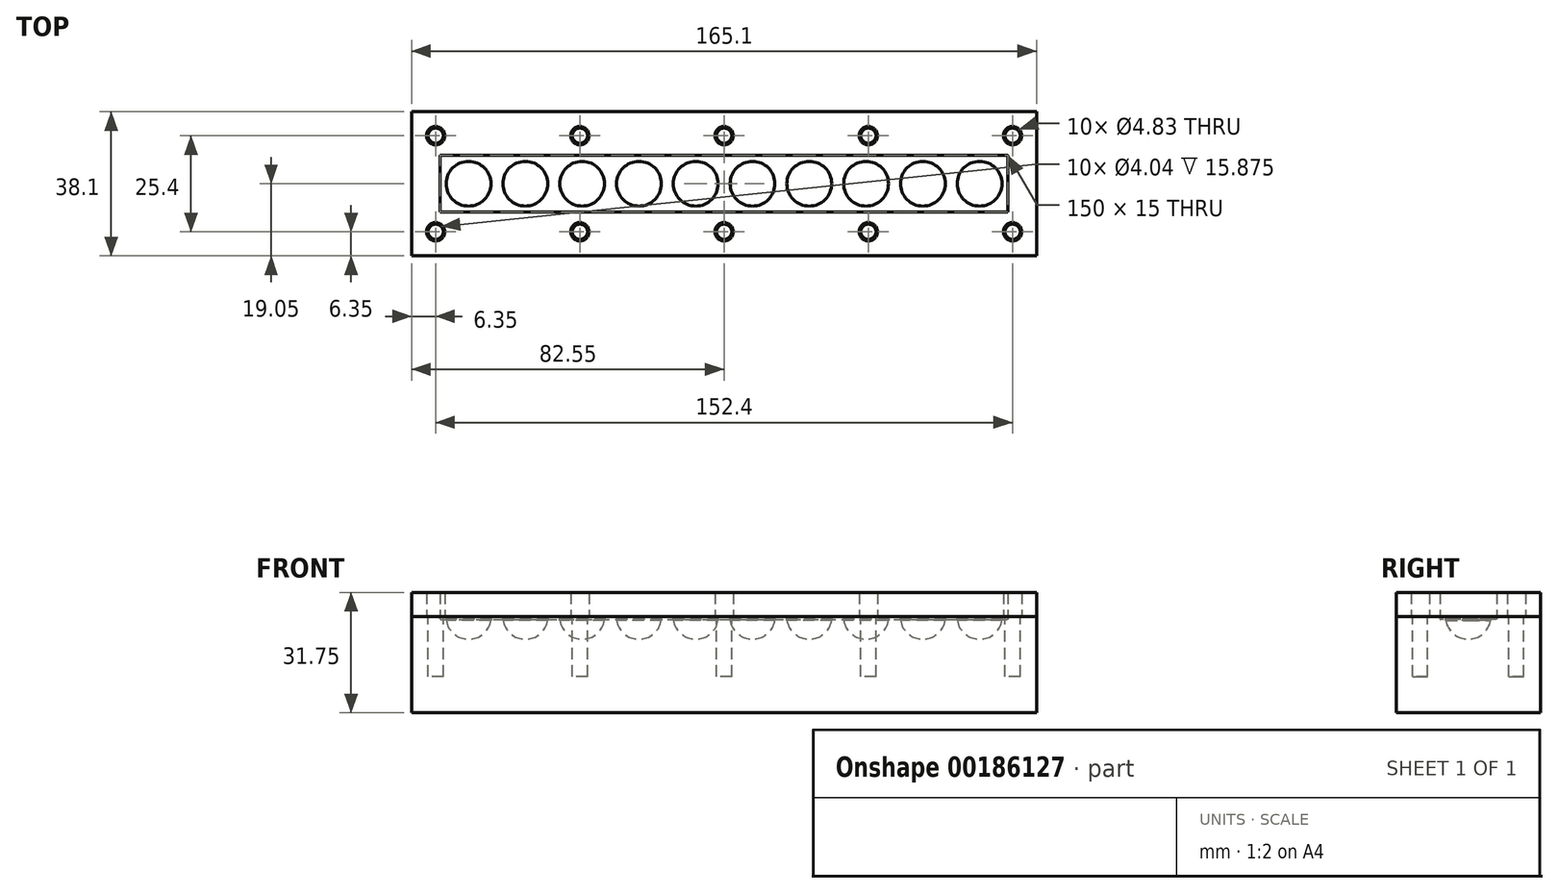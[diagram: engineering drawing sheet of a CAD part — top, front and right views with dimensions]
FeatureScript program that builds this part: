
annotation { "Feature Type Name" : "Feature", "Feature Type Description" : "" }
export const myFeature = defineFeature(function(context is Context, id is Id, definition is map)
    precondition{}
    {
        {
            var Q0;
            Q0=qCreatedBy(makeId("Top.planeOp"),FACE);
            var sketch = newSketch(context, id + "F0", { "sketchPlane" : qUnion([Q0])});
            skLineSegment(sketch, "E0.bottom", {"start": v(0, 0) * mm, "end": v(165.1, 0) * mm});
            skLineSegment(sketch, "E0.top", {"start": v(0, 38.1) * mm, "end": v(165.1, 38.1) * mm});
            skLineSegment(sketch, "E0.left", {"start": v(0, 0) * mm, "end": v(0, 38.1) * mm});
            skLineSegment(sketch, "E0.right", {"start": v(165.1, 0) * mm, "end": v(165.1, 38.1) * mm});
            skSolve(sketch);
        }
        {
            var Q0;
            Q0 = qSketchRegion(id + "F0", true);
            extrude(context, id + "F1", {"entities" : qUnion([Q0]), "depth" : 25.4 * mm});
        }
        {
            var Q0;
            Q0=makeQuery(id+"F1.opExtrude","SWEPT_FACE",FACE,{"disambiguationData":[OSD([sQuery(id+"F0.wireOp",EDGE,"E0.bottom")])]});
            var Q1;
            Q1=makeQuery(id+"F1.opExtrude","SWEPT_FACE",FACE,{"disambiguationData":[OSD([sQuery(id+"F0.wireOp",EDGE,"E0.top")])]});
            cPlane(context, id + "F2", {"entities" : qUnion([Q0, Q1]), "cplaneType" : CPlaneType.MID_PLANE, "offset" : 25.4 * mm, "width" : 152.4 * mm, "height" : 152.4 * mm});
        }
        {
            var Q0;
            Q0=qCreatedBy(id+"F2.planeOp",FACE);
            var sketch = newSketch(context, id + "F3", { "sketchPlane" : qUnion([Q0])});
            skCircle(sketch, "E1", {"center": v(15.05, 25.4) * mm, "radius": 6 * mm});
            skCircle(sketch, "E2", {"center": v(30.05, 25.4) * mm, "radius": 6 * mm});
            skCircle(sketch, "E3", {"center": v(45.05, 25.4) * mm, "radius": 6 * mm});
            skCircle(sketch, "E4", {"center": v(60.05, 25.4) * mm, "radius": 6 * mm});
            skCircle(sketch, "E5", {"center": v(75.05, 25.4) * mm, "radius": 6 * mm});
            skCircle(sketch, "E6", {"center": v(90.05, 25.4) * mm, "radius": 6 * mm});
            skCircle(sketch, "E7", {"center": v(105.05, 25.4) * mm, "radius": 6 * mm});
            skCircle(sketch, "E8", {"center": v(120.05, 25.4) * mm, "radius": 6 * mm});
            skLineSegment(sketch, "E9", {"start": v(15.05, 25.4) * mm, "end": v(30.05, 25.4) * mm, "construction": true});
            skLineSegment(sketch, "E10", {"start": v(30.05, 25.4) * mm, "end": v(45.05, 25.4) * mm, "construction": true});
            skLineSegment(sketch, "E11", {"start": v(45.05, 25.4) * mm, "end": v(60.05, 25.4) * mm, "construction": true});
            skLineSegment(sketch, "E12", {"start": v(60.05, 25.4) * mm, "end": v(75.05, 25.4) * mm, "construction": true});
            skLineSegment(sketch, "E13", {"start": v(75.05, 25.4) * mm, "end": v(90.05, 25.4) * mm, "construction": true});
            skLineSegment(sketch, "E14", {"start": v(90.05, 25.4) * mm, "end": v(105.05, 25.4) * mm, "construction": true});
            skLineSegment(sketch, "E15", {"start": v(105.05, 25.4) * mm, "end": v(120.05, 25.4) * mm, "construction": true});
            skCircle(sketch, "E16", {"center": v(135.05, 25.4) * mm, "radius": 6 * mm});
            skCircle(sketch, "E17", {"center": v(150.05, 25.4) * mm, "radius": 6 * mm});
            skLineSegment(sketch, "E18", {"start": v(120.05, 25.4) * mm, "end": v(135.05, 25.4) * mm, "construction": true});
            skLineSegment(sketch, "E19", {"start": v(135.05, 25.4) * mm, "end": v(150.05, 25.4) * mm, "construction": true});
            skLineSegment(sketch, "E20", {"start": v(0, 25.4) * mm, "end": v(15.05, 25.4) * mm, "construction": true});
            skLineSegment(sketch, "E21", {"start": v(150.05, 25.4) * mm, "end": v(165.1, 25.4) * mm, "construction": true});
            skSolve(sketch);
        }
        {
            var Q0;
            Q0=makeQuery(id+"F3.imprint","IMPRINT",FACE,{"disambiguationData":[TD([[makeQuery(id+"F3.imprint","IMPRINT",EDGE,{"derivedFrom":sQuery(id+"F3.wireOp",EDGE,"E17")}),1.0]])]});
            var Q1;
            Q1=makeQuery(id+"F3.imprint","IMPRINT",FACE,{"disambiguationData":[TD([[makeQuery(id+"F3.imprint","IMPRINT",EDGE,{"derivedFrom":sQuery(id+"F3.wireOp",EDGE,"E16")}),1.0]])]});
            var Q2;
            Q2=makeQuery(id+"F3.imprint","IMPRINT",FACE,{"disambiguationData":[TD([[makeQuery(id+"F3.imprint","IMPRINT",EDGE,{"derivedFrom":sQuery(id+"F3.wireOp",EDGE,"E8")}),1.0]])]});
            var Q3;
            Q3=makeQuery(id+"F3.imprint","IMPRINT",FACE,{"disambiguationData":[TD([[makeQuery(id+"F3.imprint","IMPRINT",EDGE,{"derivedFrom":sQuery(id+"F3.wireOp",EDGE,"E7")}),1.0]])]});
            var Q4;
            Q4=makeQuery(id+"F3.imprint","IMPRINT",FACE,{"disambiguationData":[TD([[makeQuery(id+"F3.imprint","IMPRINT",EDGE,{"derivedFrom":sQuery(id+"F3.wireOp",EDGE,"E6")}),1.0]])]});
            var Q5;
            Q5=makeQuery(id+"F3.imprint","IMPRINT",FACE,{"disambiguationData":[TD([[makeQuery(id+"F3.imprint","IMPRINT",EDGE,{"derivedFrom":sQuery(id+"F3.wireOp",EDGE,"E5")}),1.0]])]});
            var Q6;
            Q6=makeQuery(id+"F3.imprint","IMPRINT",FACE,{"disambiguationData":[TD([[makeQuery(id+"F3.imprint","IMPRINT",EDGE,{"derivedFrom":sQuery(id+"F3.wireOp",EDGE,"E4")}),1.0]])]});
            var Q7;
            Q7=makeQuery(id+"F3.imprint","IMPRINT",FACE,{"disambiguationData":[TD([[makeQuery(id+"F3.imprint","IMPRINT",EDGE,{"derivedFrom":sQuery(id+"F3.wireOp",EDGE,"E3")}),1.0]])]});
            var Q8;
            Q8=makeQuery(id+"F3.imprint","IMPRINT",FACE,{"disambiguationData":[TD([[makeQuery(id+"F3.imprint","IMPRINT",EDGE,{"derivedFrom":sQuery(id+"F3.wireOp",EDGE,"E2")}),1.0]])]});
            var Q9;
            Q9=makeQuery(id+"F3.imprint","IMPRINT",FACE,{"disambiguationData":[TD([[makeQuery(id+"F3.imprint","IMPRINT",EDGE,{"derivedFrom":sQuery(id+"F3.wireOp",EDGE,"E1")}),1.0]])]});
            extrude(context, id + "F4", {"entities" : qUnion([Q0, Q1, Q2, Q3, Q4, Q5, Q6, Q7, Q8, Q9]), "operationType" : NewBodyOperationType.REMOVE, "endBound" : BoundingType.SYMMETRIC, "oppositeDirection" : true, "depth" : 12 * mm});
        }
        {
            var Q0;
            Q0=makeQuery(id+"F4.boolean.opBoolean","COPY",EDGE,{"derivedFrom":makeQuery(id+"F4.opExtrude","CAP_EDGE",EDGE,{"disambiguationData":[OSD([sQuery(id+"F3.wireOp",EDGE,"E1")])],"isStart":false})});
            var Q1;
            Q1=makeQuery(id+"F4.boolean.opBoolean","COPY",EDGE,{"derivedFrom":makeQuery(id+"F4.opExtrude","CAP_EDGE",EDGE,{"disambiguationData":[OSD([sQuery(id+"F3.wireOp",EDGE,"E2")])],"isStart":false})});
            var Q2;
            Q2=makeQuery(id+"F4.boolean.opBoolean","COPY",EDGE,{"derivedFrom":makeQuery(id+"F4.opExtrude","CAP_EDGE",EDGE,{"disambiguationData":[OSD([sQuery(id+"F3.wireOp",EDGE,"E3")])],"isStart":false})});
            var Q3;
            Q3=makeQuery(id+"F4.boolean.opBoolean","COPY",EDGE,{"derivedFrom":makeQuery(id+"F4.opExtrude","CAP_EDGE",EDGE,{"disambiguationData":[OSD([sQuery(id+"F3.wireOp",EDGE,"E4")])],"isStart":false})});
            var Q4;
            Q4=makeQuery(id+"F4.boolean.opBoolean","COPY",EDGE,{"derivedFrom":makeQuery(id+"F4.opExtrude","CAP_EDGE",EDGE,{"disambiguationData":[OSD([sQuery(id+"F3.wireOp",EDGE,"E5")])],"isStart":false})});
            var Q5;
            Q5=makeQuery(id+"F4.boolean.opBoolean","COPY",EDGE,{"derivedFrom":makeQuery(id+"F4.opExtrude","CAP_EDGE",EDGE,{"disambiguationData":[OSD([sQuery(id+"F3.wireOp",EDGE,"E6")])],"isStart":false})});
            var Q6;
            Q6=makeQuery(id+"F4.boolean.opBoolean","COPY",EDGE,{"derivedFrom":makeQuery(id+"F4.opExtrude","CAP_EDGE",EDGE,{"disambiguationData":[OSD([sQuery(id+"F3.wireOp",EDGE,"E7")])],"isStart":false})});
            var Q7;
            Q7=makeQuery(id+"F4.boolean.opBoolean","COPY",EDGE,{"derivedFrom":makeQuery(id+"F4.opExtrude","CAP_EDGE",EDGE,{"disambiguationData":[OSD([sQuery(id+"F3.wireOp",EDGE,"E8")])],"isStart":false})});
            var Q8;
            Q8=makeQuery(id+"F4.boolean.opBoolean","COPY",EDGE,{"derivedFrom":makeQuery(id+"F4.opExtrude","CAP_EDGE",EDGE,{"disambiguationData":[OSD([sQuery(id+"F3.wireOp",EDGE,"E16")])],"isStart":false})});
            var Q9;
            Q9=makeQuery(id+"F4.boolean.opBoolean","COPY",EDGE,{"derivedFrom":makeQuery(id+"F4.opExtrude","CAP_EDGE",EDGE,{"disambiguationData":[OSD([sQuery(id+"F3.wireOp",EDGE,"E17")])],"isStart":false})});
            var Q10;
            Q10=makeQuery(id+"F4.boolean.opBoolean","COPY",EDGE,{"derivedFrom":makeQuery(id+"F4.opExtrude","CAP_EDGE",EDGE,{"disambiguationData":[OSD([sQuery(id+"F3.wireOp",EDGE,"E17")])],"isStart":true})});
            var Q11;
            Q11=makeQuery(id+"F4.boolean.opBoolean","COPY",EDGE,{"derivedFrom":makeQuery(id+"F4.opExtrude","CAP_EDGE",EDGE,{"disambiguationData":[OSD([sQuery(id+"F3.wireOp",EDGE,"E16")])],"isStart":true})});
            var Q12;
            Q12=makeQuery(id+"F4.boolean.opBoolean","COPY",EDGE,{"derivedFrom":makeQuery(id+"F4.opExtrude","CAP_EDGE",EDGE,{"disambiguationData":[OSD([sQuery(id+"F3.wireOp",EDGE,"E8")])],"isStart":true})});
            var Q13;
            Q13=makeQuery(id+"F4.boolean.opBoolean","COPY",EDGE,{"derivedFrom":makeQuery(id+"F4.opExtrude","CAP_EDGE",EDGE,{"disambiguationData":[OSD([sQuery(id+"F3.wireOp",EDGE,"E7")])],"isStart":true})});
            var Q14;
            Q14=makeQuery(id+"F4.boolean.opBoolean","COPY",EDGE,{"derivedFrom":makeQuery(id+"F4.opExtrude","CAP_EDGE",EDGE,{"disambiguationData":[OSD([sQuery(id+"F3.wireOp",EDGE,"E6")])],"isStart":true})});
            var Q15;
            Q15=makeQuery(id+"F4.boolean.opBoolean","COPY",EDGE,{"derivedFrom":makeQuery(id+"F4.opExtrude","CAP_EDGE",EDGE,{"disambiguationData":[OSD([sQuery(id+"F3.wireOp",EDGE,"E5")])],"isStart":true})});
            var Q16;
            Q16=makeQuery(id+"F4.boolean.opBoolean","COPY",EDGE,{"derivedFrom":makeQuery(id+"F4.opExtrude","CAP_EDGE",EDGE,{"disambiguationData":[OSD([sQuery(id+"F3.wireOp",EDGE,"E4")])],"isStart":true})});
            var Q17;
            Q17=makeQuery(id+"F4.boolean.opBoolean","COPY",EDGE,{"derivedFrom":makeQuery(id+"F4.opExtrude","CAP_EDGE",EDGE,{"disambiguationData":[OSD([sQuery(id+"F3.wireOp",EDGE,"E3")])],"isStart":true})});
            var Q18;
            Q18=makeQuery(id+"F4.boolean.opBoolean","COPY",EDGE,{"derivedFrom":makeQuery(id+"F4.opExtrude","CAP_EDGE",EDGE,{"disambiguationData":[OSD([sQuery(id+"F3.wireOp",EDGE,"E2")])],"isStart":true})});
            var Q19;
            Q19=makeQuery(id+"F4.boolean.opBoolean","COPY",EDGE,{"derivedFrom":makeQuery(id+"F4.opExtrude","CAP_EDGE",EDGE,{"disambiguationData":[OSD([sQuery(id+"F3.wireOp",EDGE,"E1")])],"isStart":true})});
            fillet(context, id + "F5", {"entities" : qUnion([Q0, Q1, Q2, Q3, Q4, Q5, Q6, Q7, Q8, Q9, Q10, Q11, Q12, Q13, Q14, Q15, Q16, Q17, Q18, Q19]), "radius" : 6 * mm, "tangentPropagation" : true, "allowEdgeOverflow" : false});
        }
        {
            var Q0;
            Q0=makeQuery(id+"F1.opExtrude","CAP_FACE",FACE,{"disambiguationData":[OSD([sQuery(id+"F0.wireOp",EDGE,"E0.bottom"),sQuery(id+"F0.wireOp",EDGE,"E0.top"),sQuery(id+"F0.wireOp",EDGE,"E0.left"),sQuery(id+"F0.wireOp",EDGE,"E0.right")])],"isStart":false});
            var sketch = newSketch(context, id + "F6", { "sketchPlane" : qUnion([Q0])});
            skLineSegment(sketch, "E22.bottom", {"start": v(7.55, 26.55) * mm, "end": v(157.55, 26.55) * mm});
            skLineSegment(sketch, "E22.top", {"start": v(7.55, 11.55) * mm, "end": v(157.55, 11.55) * mm});
            skLineSegment(sketch, "E22.left", {"start": v(7.55, 26.55) * mm, "end": v(7.55, 11.55) * mm});
            skLineSegment(sketch, "E22.right", {"start": v(157.55, 26.55) * mm, "end": v(157.55, 11.55) * mm});
            skLineSegment(sketch, "E23", {"start": v(0, 19.05) * mm, "end": v(7.55, 19.05) * mm, "construction": true});
            skLineSegment(sketch, "E24", {"start": v(157.55, 19.05) * mm, "end": v(165.1, 19.05) * mm, "construction": true});
            skSolve(sketch);
        }
        {
            var Q0;
            Q0 = qSketchRegion(id + "F6", true);
            extrude(context, id + "F7", {"entities" : qUnion([Q0]), "operationType" : NewBodyOperationType.REMOVE, "oppositeDirection" : true, "depth" : 0.8 * mm});
        }
        {
            var Q0;
            Q0=makeQuery(id+"F1.opExtrude","CAP_FACE",FACE,{"disambiguationData":[OSD([sQuery(id+"F0.wireOp",EDGE,"E0.bottom"),sQuery(id+"F0.wireOp",EDGE,"E0.top"),sQuery(id+"F0.wireOp",EDGE,"E0.left"),sQuery(id+"F0.wireOp",EDGE,"E0.right")])],"isStart":false});
            var sketch = newSketch(context, id + "F8", { "sketchPlane" : qUnion([Q0])});
            skCircle(sketch, "E25", {"center": v(6.35, 31.75) * mm, "radius": 2.02 * mm});
            skCircle(sketch, "E26", {"center": v(44.45, 31.75) * mm, "radius": 2.02 * mm});
            skCircle(sketch, "E27", {"center": v(82.55, 31.75) * mm, "radius": 2.02 * mm});
            skCircle(sketch, "E28", {"center": v(120.65, 31.75) * mm, "radius": 2.02 * mm});
            skCircle(sketch, "E29", {"center": v(158.75, 31.75) * mm, "radius": 2.02 * mm});
            skCircle(sketch, "E30", {"center": v(158.75, 6.35) * mm, "radius": 2.02 * mm});
            skCircle(sketch, "E31", {"center": v(120.65, 6.35) * mm, "radius": 2.02 * mm});
            skCircle(sketch, "E32", {"center": v(82.55, 6.35) * mm, "radius": 2.02 * mm});
            skCircle(sketch, "E33", {"center": v(44.45, 6.35) * mm, "radius": 2.02 * mm});
            skCircle(sketch, "E34", {"center": v(6.35, 6.35) * mm, "radius": 2.02 * mm});
            skLineSegment(sketch, "E35", {"start": v(6.35, 31.75) * mm, "end": v(6.35, 6.35) * mm, "construction": true});
            skLineSegment(sketch, "E36", {"start": v(44.45, 6.35) * mm, "end": v(44.45, 31.75) * mm, "construction": true});
            skLineSegment(sketch, "E37", {"start": v(82.55, 31.75) * mm, "end": v(82.55, 6.35) * mm, "construction": true});
            skLineSegment(sketch, "E38", {"start": v(120.65, 6.35) * mm, "end": v(120.65, 31.75) * mm, "construction": true});
            skLineSegment(sketch, "E39", {"start": v(158.75, 31.75) * mm, "end": v(158.75, 6.35) * mm, "construction": true});
            skLineSegment(sketch, "E40", {"start": v(158.75, 6.35) * mm, "end": v(120.65, 6.35) * mm, "construction": true});
            skLineSegment(sketch, "E41", {"start": v(120.65, 31.75) * mm, "end": v(158.75, 31.75) * mm, "construction": true});
            skLineSegment(sketch, "E42", {"start": v(120.65, 31.75) * mm, "end": v(82.55, 31.75) * mm, "construction": true});
            skLineSegment(sketch, "E43", {"start": v(82.55, 31.75) * mm, "end": v(44.45, 31.75) * mm, "construction": true});
            skLineSegment(sketch, "E44", {"start": v(44.45, 31.75) * mm, "end": v(6.35, 31.75) * mm, "construction": true});
            skLineSegment(sketch, "E45", {"start": v(6.35, 6.35) * mm, "end": v(44.45, 6.35) * mm, "construction": true});
            skLineSegment(sketch, "E46", {"start": v(44.45, 6.35) * mm, "end": v(82.55, 6.35) * mm, "construction": true});
            skLineSegment(sketch, "E47", {"start": v(82.55, 6.35) * mm, "end": v(120.65, 6.35) * mm, "construction": true});
            skLineSegment(sketch, "E48", {"start": v(165.1, 19.05) * mm, "end": v(158.75, 19.05) * mm, "construction": true});
            skLineSegment(sketch, "E49", {"start": v(6.35, 19.05) * mm, "end": v(0, 19.05) * mm, "construction": true});
            skSolve(sketch);
        }
        {
            var Q0;
            Q0 = qSketchRegion(id + "F8", true);
            extrude(context, id + "F9", {"entities" : qUnion([Q0]), "operationType" : NewBodyOperationType.REMOVE, "oppositeDirection" : true, "depth" : 15.88 * mm});
        }
        {
            var Q0;
            Q0=makeQuery(id+"F7.boolean.opBoolean","INTERSECT",EDGE,{"derivedFrom":[makeQuery(id+"F5.opFillet","BLEND_FACE",FACE,{"disambiguationData":[OSD([sQuery(id+"F3.wireOp",EDGE,"E1")])]}),makeQuery(id+"F7.opExtrude","CAP_FACE",FACE,{"disambiguationData":[OSD([sQuery(id+"F6.wireOp",EDGE,"E22.bottom"),sQuery(id+"F6.wireOp",EDGE,"E22.top"),sQuery(id+"F6.wireOp",EDGE,"E22.left"),sQuery(id+"F6.wireOp",EDGE,"E22.right")])],"isStart":false})]});
            var Q1;
            Q1=makeQuery(id+"F7.boolean.opBoolean","INTERSECT",EDGE,{"derivedFrom":[makeQuery(id+"F5.opFillet","BLEND_FACE",FACE,{"disambiguationData":[OSD([sQuery(id+"F3.wireOp",EDGE,"E2")])]}),makeQuery(id+"F7.opExtrude","CAP_FACE",FACE,{"disambiguationData":[OSD([sQuery(id+"F6.wireOp",EDGE,"E22.bottom"),sQuery(id+"F6.wireOp",EDGE,"E22.top"),sQuery(id+"F6.wireOp",EDGE,"E22.left"),sQuery(id+"F6.wireOp",EDGE,"E22.right")])],"isStart":false})]});
            var Q2;
            Q2=makeQuery(id+"F7.boolean.opBoolean","INTERSECT",EDGE,{"derivedFrom":[makeQuery(id+"F5.opFillet","BLEND_FACE",FACE,{"disambiguationData":[OSD([sQuery(id+"F3.wireOp",EDGE,"E3")])]}),makeQuery(id+"F7.opExtrude","CAP_FACE",FACE,{"disambiguationData":[OSD([sQuery(id+"F6.wireOp",EDGE,"E22.bottom"),sQuery(id+"F6.wireOp",EDGE,"E22.top"),sQuery(id+"F6.wireOp",EDGE,"E22.left"),sQuery(id+"F6.wireOp",EDGE,"E22.right")])],"isStart":false})]});
            var Q3;
            Q3=makeQuery(id+"F7.boolean.opBoolean","INTERSECT",EDGE,{"derivedFrom":[makeQuery(id+"F5.opFillet","BLEND_FACE",FACE,{"disambiguationData":[OSD([sQuery(id+"F3.wireOp",EDGE,"E4")])]}),makeQuery(id+"F7.opExtrude","CAP_FACE",FACE,{"disambiguationData":[OSD([sQuery(id+"F6.wireOp",EDGE,"E22.bottom"),sQuery(id+"F6.wireOp",EDGE,"E22.top"),sQuery(id+"F6.wireOp",EDGE,"E22.left"),sQuery(id+"F6.wireOp",EDGE,"E22.right")])],"isStart":false})]});
            var Q4;
            Q4=makeQuery(id+"F7.boolean.opBoolean","INTERSECT",EDGE,{"derivedFrom":[makeQuery(id+"F5.opFillet","BLEND_FACE",FACE,{"disambiguationData":[OSD([sQuery(id+"F3.wireOp",EDGE,"E5")])]}),makeQuery(id+"F7.opExtrude","CAP_FACE",FACE,{"disambiguationData":[OSD([sQuery(id+"F6.wireOp",EDGE,"E22.bottom"),sQuery(id+"F6.wireOp",EDGE,"E22.top"),sQuery(id+"F6.wireOp",EDGE,"E22.left"),sQuery(id+"F6.wireOp",EDGE,"E22.right")])],"isStart":false})]});
            var Q5;
            Q5=makeQuery(id+"F7.boolean.opBoolean","INTERSECT",EDGE,{"derivedFrom":[makeQuery(id+"F5.opFillet","BLEND_FACE",FACE,{"disambiguationData":[OSD([sQuery(id+"F3.wireOp",EDGE,"E6")])]}),makeQuery(id+"F7.opExtrude","CAP_FACE",FACE,{"disambiguationData":[OSD([sQuery(id+"F6.wireOp",EDGE,"E22.bottom"),sQuery(id+"F6.wireOp",EDGE,"E22.top"),sQuery(id+"F6.wireOp",EDGE,"E22.left"),sQuery(id+"F6.wireOp",EDGE,"E22.right")])],"isStart":false})]});
            var Q6;
            Q6=makeQuery(id+"F7.boolean.opBoolean","INTERSECT",EDGE,{"derivedFrom":[makeQuery(id+"F5.opFillet","BLEND_FACE",FACE,{"disambiguationData":[OSD([sQuery(id+"F3.wireOp",EDGE,"E7")])]}),makeQuery(id+"F7.opExtrude","CAP_FACE",FACE,{"disambiguationData":[OSD([sQuery(id+"F6.wireOp",EDGE,"E22.bottom"),sQuery(id+"F6.wireOp",EDGE,"E22.top"),sQuery(id+"F6.wireOp",EDGE,"E22.left"),sQuery(id+"F6.wireOp",EDGE,"E22.right")])],"isStart":false})]});
            var Q7;
            Q7=makeQuery(id+"F7.boolean.opBoolean","INTERSECT",EDGE,{"derivedFrom":[makeQuery(id+"F5.opFillet","BLEND_FACE",FACE,{"disambiguationData":[OSD([sQuery(id+"F3.wireOp",EDGE,"E8")])]}),makeQuery(id+"F7.opExtrude","CAP_FACE",FACE,{"disambiguationData":[OSD([sQuery(id+"F6.wireOp",EDGE,"E22.bottom"),sQuery(id+"F6.wireOp",EDGE,"E22.top"),sQuery(id+"F6.wireOp",EDGE,"E22.left"),sQuery(id+"F6.wireOp",EDGE,"E22.right")])],"isStart":false})]});
            var Q8;
            Q8=makeQuery(id+"F7.boolean.opBoolean","INTERSECT",EDGE,{"derivedFrom":[makeQuery(id+"F5.opFillet","BLEND_FACE",FACE,{"disambiguationData":[OSD([sQuery(id+"F3.wireOp",EDGE,"E16")])]}),makeQuery(id+"F7.opExtrude","CAP_FACE",FACE,{"disambiguationData":[OSD([sQuery(id+"F6.wireOp",EDGE,"E22.bottom"),sQuery(id+"F6.wireOp",EDGE,"E22.top"),sQuery(id+"F6.wireOp",EDGE,"E22.left"),sQuery(id+"F6.wireOp",EDGE,"E22.right")])],"isStart":false})]});
            var Q9;
            Q9=makeQuery(id+"F7.boolean.opBoolean","INTERSECT",EDGE,{"derivedFrom":[makeQuery(id+"F5.opFillet","BLEND_FACE",FACE,{"disambiguationData":[OSD([sQuery(id+"F3.wireOp",EDGE,"E17")])]}),makeQuery(id+"F7.opExtrude","CAP_FACE",FACE,{"disambiguationData":[OSD([sQuery(id+"F6.wireOp",EDGE,"E22.bottom"),sQuery(id+"F6.wireOp",EDGE,"E22.top"),sQuery(id+"F6.wireOp",EDGE,"E22.left"),sQuery(id+"F6.wireOp",EDGE,"E22.right")])],"isStart":false})]});
            var Q10;
            Q10=makeQuery(id+"F7.boolean.opBoolean","INTERSECT",EDGE,{"derivedFrom":[makeQuery(id+"F5.opFillet","BLEND_FACE",FACE,{"disambiguationData":[OSD([sQuery(id+"F3.wireOp",EDGE,"E16")])]}),makeQuery(id+"F7.opExtrude","CAP_FACE",FACE,{"disambiguationData":[OSD([sQuery(id+"F6.wireOp",EDGE,"E22.bottom"),sQuery(id+"F6.wireOp",EDGE,"E22.top"),sQuery(id+"F6.wireOp",EDGE,"E22.left"),sQuery(id+"F6.wireOp",EDGE,"E22.right")])],"isStart":false})]});
            var Q11;
            Q11=makeQuery(id+"F7.boolean.opBoolean","COPY",EDGE,{"derivedFrom":makeQuery(id+"F7.opExtrude","CAP_EDGE",EDGE,{"disambiguationData":[OSD([sQuery(id+"F6.wireOp",EDGE,"E22.bottom")])],"isStart":false})});
            var Q12;
            Q12=makeQuery(id+"F7.boolean.opBoolean","COPY",EDGE,{"derivedFrom":makeQuery(id+"F7.opExtrude","CAP_EDGE",EDGE,{"disambiguationData":[OSD([sQuery(id+"F6.wireOp",EDGE,"E22.right")])],"isStart":false})});
            var Q13;
            Q13=makeQuery(id+"F7.boolean.opBoolean","COPY",EDGE,{"derivedFrom":makeQuery(id+"F7.opExtrude","CAP_EDGE",EDGE,{"disambiguationData":[OSD([sQuery(id+"F6.wireOp",EDGE,"E22.top")])],"isStart":false})});
            var Q14;
            Q14=makeQuery(id+"F7.boolean.opBoolean","COPY",EDGE,{"derivedFrom":makeQuery(id+"F7.opExtrude","CAP_EDGE",EDGE,{"disambiguationData":[OSD([sQuery(id+"F6.wireOp",EDGE,"E22.left")])],"isStart":false})});
            fillet(context, id + "F10", {"entities" : qUnion([Q0, Q1, Q2, Q3, Q4, Q5, Q6, Q7, Q8, Q9, Q10, Q11, Q12, Q13, Q14]), "radius" : 0.25 * mm, "tangentPropagation" : true, "allowEdgeOverflow" : false});
        }
        {
            var Q0;
            Q0=makeQuery(id+"F1.opExtrude","CAP_FACE",FACE,{"disambiguationData":[OSD([sQuery(id+"F0.wireOp",EDGE,"E0.bottom"),sQuery(id+"F0.wireOp",EDGE,"E0.top"),sQuery(id+"F0.wireOp",EDGE,"E0.left"),sQuery(id+"F0.wireOp",EDGE,"E0.right")])],"isStart":false});
            var sketch = newSketch(context, id + "F11", { "sketchPlane" : qUnion([Q0])});
            skLineSegment(sketch, "E50.bottom", {"start": v(165.1, 0) * mm, "end": v(0, 0) * mm});
            skLineSegment(sketch, "E50.top", {"start": v(165.1, 38.1) * mm, "end": v(0, 38.1) * mm});
            skLineSegment(sketch, "E50.left", {"start": v(165.1, 0) * mm, "end": v(165.1, 38.1) * mm});
            skLineSegment(sketch, "E50.right", {"start": v(0, 0) * mm, "end": v(0, 38.1) * mm});
            skCircle(sketch, "E51", {"center": v(158.75, 6.35) * mm, "radius": 2.41 * mm});
            skCircle(sketch, "E52", {"center": v(120.65, 6.35) * mm, "radius": 2.41 * mm});
            skCircle(sketch, "E53", {"center": v(82.55, 6.35) * mm, "radius": 2.41 * mm});
            skCircle(sketch, "E54", {"center": v(44.45, 6.35) * mm, "radius": 2.41 * mm});
            skCircle(sketch, "E55", {"center": v(6.35, 6.35) * mm, "radius": 2.41 * mm});
            skCircle(sketch, "E56", {"center": v(6.35, 31.75) * mm, "radius": 2.41 * mm});
            skCircle(sketch, "E57", {"center": v(44.45, 31.75) * mm, "radius": 2.41 * mm});
            skCircle(sketch, "E58", {"center": v(82.55, 31.75) * mm, "radius": 2.41 * mm});
            skCircle(sketch, "E59", {"center": v(120.65, 31.75) * mm, "radius": 2.41 * mm});
            skCircle(sketch, "E60", {"center": v(158.75, 31.75) * mm, "radius": 2.41 * mm});
            skSolve(sketch);
        }
        {
            var Q0;
            Q0=makeQuery(id+"F11.imprint","IMPRINT",FACE,{"disambiguationData":[TD([[makeQuery(id+"F11.imprint","IMPRINT",EDGE,{"derivedFrom":sQuery(id+"F11.wireOp",EDGE,"E50.bottom")}),1.0]])]});
            var Q1;
            Q1=makeQuery(id+"F11.imprint","IMPRINT",FACE,{"disambiguationData":[TD([[makeQuery(id+"F11.imprint","IMPRINT",EDGE,{"derivedFrom":makeQuery(id+"F7.boolean.opBoolean","COPY",EDGE,{"derivedFrom":makeQuery(id+"F7.opExtrude","CAP_EDGE",EDGE,{"disambiguationData":[OSD([sQuery(id+"F6.wireOp",EDGE,"E22.bottom")])],"isStart":true})})}),-1.0]])]});
            extrude(context, id + "F12", {"entities" : qUnion([Q0, Q1]), "depth" : 6.35 * mm});
        }
    });
